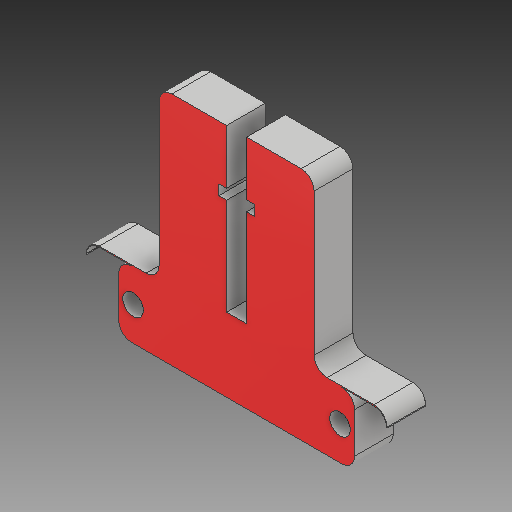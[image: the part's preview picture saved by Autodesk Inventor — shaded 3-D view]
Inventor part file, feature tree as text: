
AUTODESK INVENTOR PART (.ipt)
format: ipt  version: 2017 (Build 210142000, 142)  size: 177,664 bytes
history: native  units: mm
features: sketch x6, other x3
ambient origin geometry x8: Origin, YZ Plane, XZ Plane, XY Plane, X Axis, Y Axis, Z Axis, Center Point
bodies: Solid1 (feature_tree)
feature tree (9):
  other  "Hotend Slide Part 1_MIR.ipt"
  other  "Solid1::Hotend Slide Part 1_MIR.ipt"
  other  "TaggingFeature1"
  sketch  "Sketch1"  dims[d0=10.0mm]
  sketch  "Sketch2"
  sketch  "Sketch3"
  sketch  "Sketch4"
  sketch  "Sketch5"
  sketch  "Sketch6"
